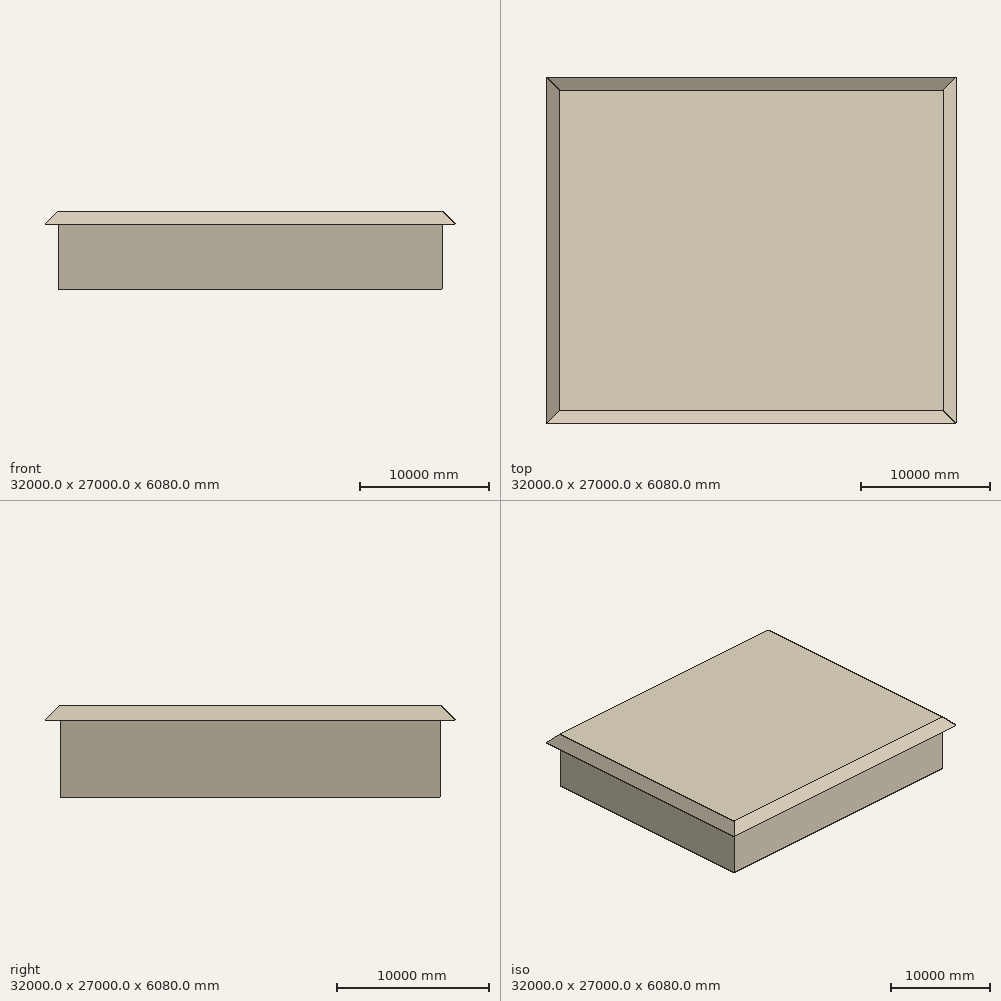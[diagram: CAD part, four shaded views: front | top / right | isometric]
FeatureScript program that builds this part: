
annotation { "Feature Type Name" : "Feature", "Feature Type Description" : "" }
export const myFeature = defineFeature(function(context is Context, id is Id, definition is map)
    precondition{}
    {
        {
            var Q0;
            Q0=qCreatedBy(makeId("Top.planeOp"),FACE);
            var sketch = newSketch(context, id + "F0", { "sketchPlane" : qUnion([Q0])});
            skLineSegment(sketch, "E0.bottom", {"start": v(-14985.35, -8854.44) * mm, "end": v(15014.65, -8854.44) * mm});
            skLineSegment(sketch, "E0.top", {"start": v(-14985.35, 16145.56) * mm, "end": v(15014.65, 16145.56) * mm});
            skLineSegment(sketch, "E0.left", {"start": v(-14985.35, -8854.44) * mm, "end": v(-14985.35, 16145.56) * mm});
            skLineSegment(sketch, "E0.right", {"start": v(15014.65, -8854.44) * mm, "end": v(15014.65, 16145.56) * mm});
            skSolve(sketch);
        }
        {
            var Q0;
            Q0=makeQuery(id+"F0.imprint","IMPRINT",FACE,{"disambiguationData":[TD([[makeQuery(id+"F0.imprint","IMPRINT",EDGE,{"derivedFrom":sQuery(id+"F0.wireOp",EDGE,"E0.bottom")}),1.0]])]});
            extrude(context, id + "F1", {"entities" : qUnion([Q0]), "depth" : 5080 * mm});
        }
        {
            var Q0;
            Q0=makeQuery(id+"F1.opExtrude","CAP_FACE",FACE,{"disambiguationData":[OSD([sQuery(id+"F0.wireOp",EDGE,"E0.bottom"),sQuery(id+"F0.wireOp",EDGE,"E0.top"),sQuery(id+"F0.wireOp",EDGE,"E0.left"),sQuery(id+"F0.wireOp",EDGE,"E0.right")])],"isStart":false});
            var sketch = newSketch(context, id + "F2", { "sketchPlane" : qUnion([Q0])});
            skLineSegment(sketch, "E1.bottom", {"start": v(-15985.35, -9854.44) * mm, "end": v(16014.65, -9854.44) * mm});
            skLineSegment(sketch, "E1.top", {"start": v(-15985.35, 17145.56) * mm, "end": v(16014.65, 17145.56) * mm});
            skLineSegment(sketch, "E1.left", {"start": v(-15985.35, -9854.44) * mm, "end": v(-15985.35, 17145.56) * mm});
            skLineSegment(sketch, "E1.right", {"start": v(16014.65, -9854.44) * mm, "end": v(16014.65, 17145.56) * mm});
            skSolve(sketch);
        }
        {
            var Q0;
            Q0 = qSketchRegion(id + "F2", true);
            extrude(context, id + "F3", {"entities" : qUnion([Q0]), "operationType" : NewBodyOperationType.ADD, "depth" : 1000 * mm});
        }
        {
            var Q0;
            Q0=makeQuery(id+"F3.opExtrude","CAP_EDGE",EDGE,{"disambiguationData":[OSD([sQuery(id+"F2.wireOp",EDGE,"E1.bottom")])],"isStart":false});
            var Q1;
            Q1=makeQuery(id+"F3.opExtrude","CAP_EDGE",EDGE,{"disambiguationData":[OSD([sQuery(id+"F2.wireOp",EDGE,"E1.right")])],"isStart":false});
            var Q2;
            Q2=makeQuery(id+"F3.opExtrude","CAP_EDGE",EDGE,{"disambiguationData":[OSD([sQuery(id+"F2.wireOp",EDGE,"E1.top")])],"isStart":false});
            var Q3;
            Q3=makeQuery(id+"F3.opExtrude","CAP_EDGE",EDGE,{"disambiguationData":[OSD([sQuery(id+"F2.wireOp",EDGE,"E1.left")])],"isStart":false});
            chamfer(context, id + "F4", {"entities" : qUnion([Q0, Q1, Q2, Q3]), "width" : 1000 * mm, "tangentPropagation" : true});
        }
    });
